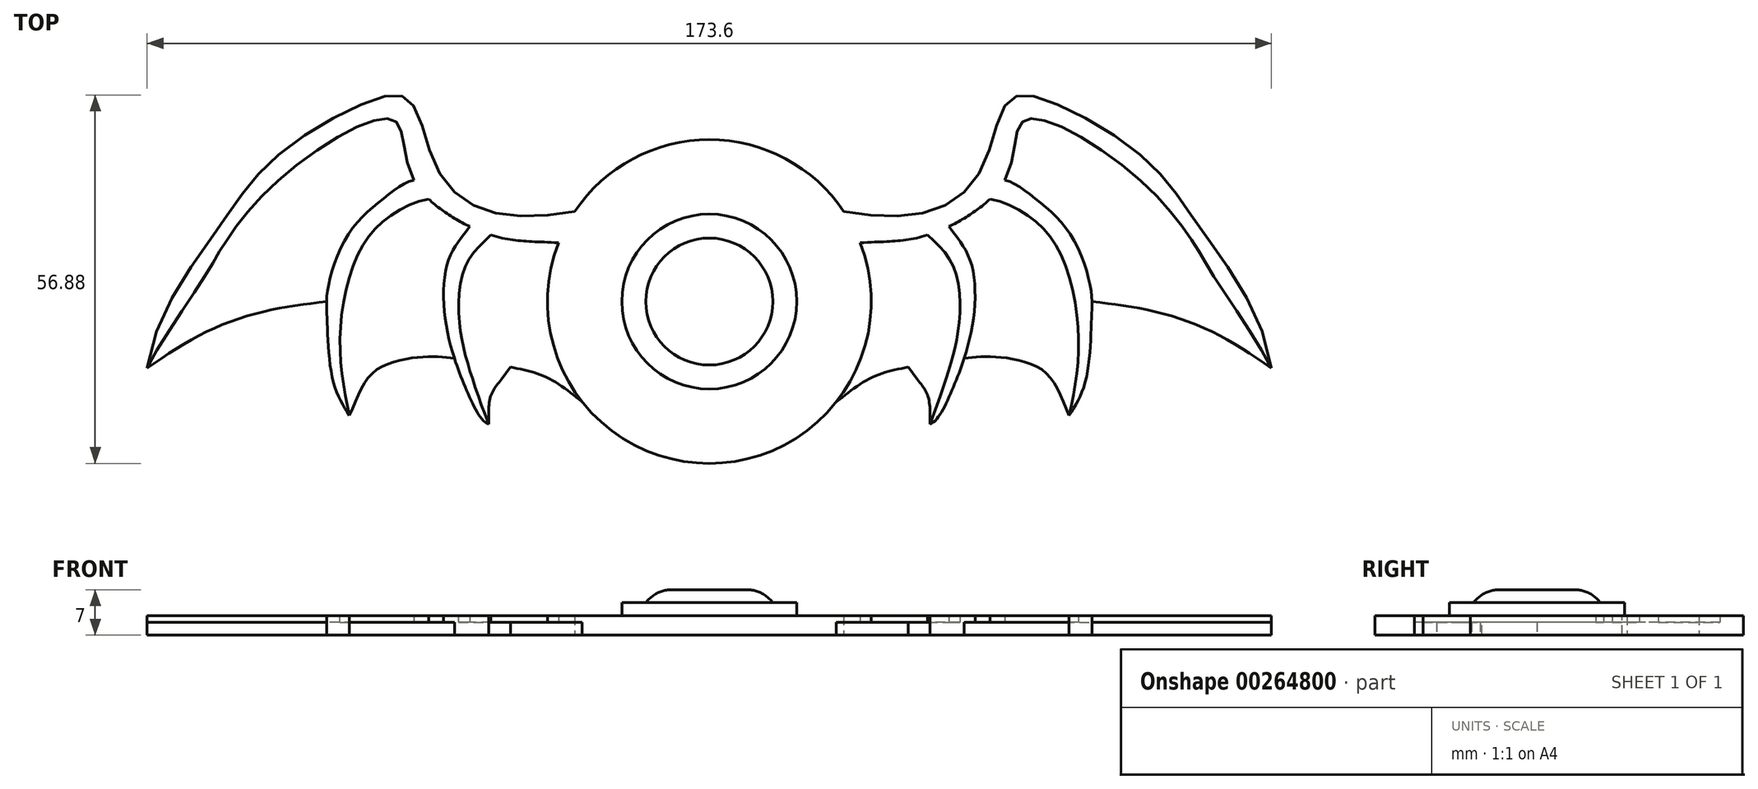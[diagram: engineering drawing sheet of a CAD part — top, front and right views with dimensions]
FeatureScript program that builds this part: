
annotation { "Feature Type Name" : "Feature", "Feature Type Description" : "" }
export const myFeature = defineFeature(function(context is Context, id is Id, definition is map)
    precondition{}
    {
        {
            var Q0;
            Q0=qCreatedBy(makeId("Top.planeOp"),FACE);
            var sketch = newSketch(context, id + "F0", { "sketchPlane" : qUnion([Q0])});
            skCircle(sketch, "E0", {"center": v(0, 0) * mm, "radius": 25 * mm});
            skLineSegment(sketch, "E1", {"start": v(0, 25) * mm, "end": v(0, -25) * mm, "construction": true});
            skFitSpline(sketch, "E2", {"points": [v(20.76, 13.92) * mm, v(34.08, 13.92) * mm, v(42, 20.48) * mm, v(46, 30.69) * mm, v(50.93, 31.48) * mm, v(67.03, 22.24) * mm, v(75.74, 11.46) * mm, v(86.8, -10.28) * mm], "startDerivative": vector(95.75, -17.53) * mm, "endDerivative": vector(18.54, -135.11) * mm});
            skFitSpline(sketch, "E3", {"points": [v(20.7, -14) * mm, v(37, -10.54) * mm, v(45, -8.07) * mm, v(66.66, 1.74) * mm, v(75.74, 11.46) * mm], "startDerivative": vector(59.46, -0.59) * mm, "endDerivative": vector(18.77, 28.66) * mm, "construction": true});
            skFitSpline(sketch, "E4", {"points": [v(23.3, 9.08) * mm, v(33.72, 10.28) * mm, v(45.64, 18.76) * mm, v(47.9, 27.18) * mm, v(51.1, 28.14) * mm, v(65.44, 19.69) * mm, v(74.45, 9.58) * mm, v(78.2, 3.43) * mm, v(86.8, -10.28) * mm], "startDerivative": vector(110.38, 5.87) * mm, "endDerivative": vector(40.39, -81.17) * mm});
            skFitSpline(sketch, "E5", {"points": [v(33.72, 10.28) * mm, v(37.86, 5.02) * mm, v(38.5, -3.9) * mm, v(37, -10.54) * mm, v(34.08, -18.9) * mm], "startDerivative": vector(21.3, -19.5) * mm, "endDerivative": vector(-13.55, -34.2) * mm});
            skFitSpline(sketch, "E6", {"points": [v(37, 11.6) * mm, v(40.25, 6.46) * mm, v(40.52, -4.24) * mm, v(37.2, -14.33) * mm, v(34.08, -18.9) * mm], "startDerivative": vector(14.85, -22) * mm, "endDerivative": vector(-16.96, -5.17) * mm});
            skFitSpline(sketch, "E7", {"points": [v(32.11, -12.01) * mm, v(33.72, -14.49) * mm, v(34.08, -18.9) * mm], "startDerivative": vector(4.43, -5.79) * mm, "endDerivative": vector(-0.15, -8.8) * mm});
            skFitSpline(sketch, "E8", {"points": [v(45.64, 18.76) * mm, v(50.26, 15.97) * mm, v(55.72, 10.44) * mm, v(58.9, 2) * mm, v(59.02, -2.64) * mm, v(58.1, -12.2) * mm, v(55.56, -17.62) * mm], "startDerivative": vector(28.21, -5.42) * mm, "endDerivative": vector(-19.1, -30.2) * mm});
            skFitSpline(sketch, "E9", {"points": [v(43.34, 15.84) * mm, v(49.55, 13.02) * mm, v(53.96, 7.9) * mm, v(56.67, -1.36) * mm, v(56.83, -10.28) * mm, v(55.56, -17.62) * mm], "startDerivative": vector(32.47, -4.35) * mm, "endDerivative": vector(-7.91, -36.84) * mm});
            skFitSpline(sketch, "E10", {"points": [v(38.97, -9.94) * mm, v(46.63, -10.28) * mm, v(52.84, -13.22) * mm, v(55.56, -17.62) * mm], "startDerivative": vector(21.38, 0.7) * mm, "endDerivative": vector(7.12, -15.9) * mm, "construction": true});
            skFitSpline(sketch, "E11", {"points": [v(59.1, 0) * mm, v(68, -1.36) * mm, v(77.72, -4.7) * mm, v(86.8, -10.28) * mm], "startDerivative": vector(27.78, -3.23) * mm, "endDerivative": vector(25.67, -17.5) * mm});
            skFitSpline(sketch, "E12", {"points": [v(19.62, -15.5) * mm, v(25.1, -11.72) * mm, v(30.69, -10.12) * mm], "startDerivative": vector(10.4, 8.3) * mm, "endDerivative": vector(11.78, 2.35) * mm});
            skFitSpline(sketch, "E13", {"points": [v(32.11, -12.01) * mm, v(30.69, -10.12) * mm], "startDerivative": vector(-1.42, 1.9) * mm, "endDerivative": vector(-1.42, 1.9) * mm});
            skFitSpline(sketch, "E14", {"points": [v(55.56, -17.62) * mm, v(52.05, -11.08) * mm, v(46.6, -8.83) * mm, v(42.13, -8.5) * mm, v(39.36, -8.79) * mm], "startDerivative": vector(-10.96, 25.87) * mm, "endDerivative": vector(-14.04, -2.02) * mm});
            skFitSpline(sketch, "E15", {"points": [v(20.76, 13.92) * mm, v(16.18, 9.49) * mm, v(19.62, -15.5) * mm], "startDerivative": vector(-16.85, -9.2) * mm, "endDerivative": vector(11.44, -45.62) * mm});
            skFitSpline(sketch, "E16.MirrorCS", {"points": [v(-20.76, 13.92) * mm, v(-16.18, 9.49) * mm, v(-19.62, -15.5) * mm], "startDerivative": vector(16.85, -9.2) * mm, "endDerivative": vector(-11.44, -45.62) * mm});
            skFitSpline(sketch, "E17.MirrorCS", {"points": [v(-23.3, 9.08) * mm, v(-33.72, 10.28) * mm, v(-45.64, 18.76) * mm, v(-47.9, 27.18) * mm, v(-51.1, 28.14) * mm, v(-65.44, 19.69) * mm, v(-74.45, 9.58) * mm, v(-78.2, 3.43) * mm, v(-86.8, -10.28) * mm], "startDerivative": vector(-110.38, 5.87) * mm, "endDerivative": vector(-40.39, -81.17) * mm});
            skFitSpline(sketch, "E18.MirrorCS", {"points": [v(-20.76, 13.92) * mm, v(-34.08, 13.92) * mm, v(-42, 20.48) * mm, v(-46, 30.69) * mm, v(-50.93, 31.48) * mm, v(-67.03, 22.24) * mm, v(-75.74, 11.46) * mm, v(-86.8, -10.28) * mm], "startDerivative": vector(-95.75, -17.53) * mm, "endDerivative": vector(-18.54, -135.11) * mm});
            skFitSpline(sketch, "E19.MirrorCS", {"points": [v(-33.72, 10.28) * mm, v(-37.86, 5.02) * mm, v(-38.5, -3.9) * mm, v(-37, -10.54) * mm, v(-34.08, -18.9) * mm], "startDerivative": vector(-21.3, -19.5) * mm, "endDerivative": vector(13.55, -34.2) * mm});
            skFitSpline(sketch, "E20.MirrorCS", {"points": [v(-37, 11.6) * mm, v(-40.25, 6.46) * mm, v(-40.52, -4.24) * mm, v(-37.2, -14.33) * mm, v(-34.08, -18.9) * mm], "startDerivative": vector(-14.85, -22) * mm, "endDerivative": vector(16.96, -5.17) * mm});
            skFitSpline(sketch, "E21.MirrorCS", {"points": [v(-43.34, 15.84) * mm, v(-49.55, 13.02) * mm, v(-53.96, 7.9) * mm, v(-56.67, -1.36) * mm, v(-56.83, -10.28) * mm, v(-55.56, -17.62) * mm], "startDerivative": vector(-32.47, -4.35) * mm, "endDerivative": vector(7.91, -36.84) * mm});
            skFitSpline(sketch, "E22.MirrorCS", {"points": [v(-45.64, 18.76) * mm, v(-50.26, 15.97) * mm, v(-55.72, 10.44) * mm, v(-58.9, 2) * mm, v(-59.02, -2.64) * mm, v(-58.1, -12.2) * mm, v(-55.56, -17.62) * mm], "startDerivative": vector(-28.21, -5.42) * mm, "endDerivative": vector(19.1, -30.2) * mm});
            skFitSpline(sketch, "E23.MirrorCS", {"points": [v(-19.62, -15.5) * mm, v(-25.1, -11.72) * mm, v(-30.69, -10.12) * mm], "startDerivative": vector(-10.4, 8.3) * mm, "endDerivative": vector(-11.78, 2.35) * mm});
            skFitSpline(sketch, "E24.MirrorCS", {"points": [v(-32.11, -12.01) * mm, v(-30.69, -10.12) * mm], "startDerivative": vector(1.42, 1.9) * mm, "endDerivative": vector(1.42, 1.9) * mm});
            skFitSpline(sketch, "E25.MirrorCS", {"points": [v(-32.11, -12.01) * mm, v(-33.72, -14.49) * mm, v(-34.08, -18.9) * mm], "startDerivative": vector(-4.43, -5.79) * mm, "endDerivative": vector(0.15, -8.8) * mm});
            skFitSpline(sketch, "E26.MirrorCS", {"points": [v(-59.1, 0) * mm, v(-68, -1.36) * mm, v(-77.72, -4.7) * mm, v(-86.8, -10.28) * mm], "startDerivative": vector(-27.78, -3.23) * mm, "endDerivative": vector(-25.67, -17.5) * mm});
            skFitSpline(sketch, "E27.MirrorCS", {"points": [v(-55.56, -17.62) * mm, v(-52.05, -11.08) * mm, v(-46.6, -8.83) * mm, v(-42.13, -8.5) * mm, v(-39.36, -8.79) * mm], "startDerivative": vector(10.96, 25.87) * mm, "endDerivative": vector(14.04, -2.02) * mm});
            skSolve(sketch);
        }
        {
            var Q0;
            {var subQ0=sQuery(id+"F0.wireOp",EDGE,"E15");Q0=makeQuery(id+"F0.imprint","IMPRINT",FACE,{"disambiguationData":[TD([[makeQuery(id+"F0.imprint","IMPRINT",EDGE,{"derivedFrom":subQ0}),-1.0]])]});}
            var Q1;
            {var subQ0=sQuery(id+"F0.wireOp",EDGE,"E15");Q1=makeQuery(id+"F0.imprint","IMPRINT",FACE,{"disambiguationData":[TD([[makeQuery(id+"F0.imprint","IMPRINT",EDGE,{"derivedFrom":subQ0}),1.0]])]});}
            var Q2;
            {var subQ0=sQuery(id+"F0.wireOp",EDGE,"E16.MirrorCS");Q2=makeQuery(id+"F0.imprint","IMPRINT",FACE,{"disambiguationData":[TD([[makeQuery(id+"F0.imprint","IMPRINT",EDGE,{"derivedFrom":subQ0}),-1.0]])]});}
            extrude(context, id + "F1", {"entities" : qUnion([Q0, Q1, Q2]), "depth" : 3 * mm, "offsetDistance" : 25 * mm});
        }
        {
            var Q0;
            Q0=qCreatedBy(makeId("Top.planeOp"),FACE);
            var sketch = newSketch(context, id + "F2", { "sketchPlane" : qUnion([Q0])});
            skCircle(sketch, "E28", {"center": v(0, 0) * mm, "radius": 13.5 * mm});
            skSolve(sketch);
        }
        {
            var Q0;
            Q0 = qSketchRegion(id + "F2", true);
            extrude(context, id + "F3", {"entities" : qUnion([Q0]), "operationType" : NewBodyOperationType.ADD, "depth" : 5 * mm, "offsetDistance" : 25 * mm});
        }
        {
            var Q0;
            Q0=qCreatedBy(makeId("Top.planeOp"),FACE);
            var sketch = newSketch(context, id + "F4", { "sketchPlane" : qUnion([Q0])});
            skCircle(sketch, "E29", {"center": v(0, 0) * mm, "radius": 9.8 * mm});
            skSolve(sketch);
        }
        {
            var Q0;
            Q0 = qSketchRegion(id + "F4", true);
            var Q1;
            Q1 = qConstructionFilter(qBodyType(qCreatedBy(id + "F4" ,EDGE), BodyType.WIRE), ConstructionObject.NO);
            extrude(context, id + "F5", {"entities" : qUnion([Q0]), "operationType" : NewBodyOperationType.ADD, "surfaceEntities" : qUnion([Q1]), "depth" : 7 * mm, "offsetDistance" : 25 * mm});
        }
        {
            var Q0;
            Q0=makeQuery(id+"F5.opExtrude","CAP_FACE",FACE,{"disambiguationData":[OSD([sQuery(id+"F4.wireOp",EDGE,"E29")])],"isStart":false});
            fillet(context, id + "F6", {"entities" : qUnion([Q0]), "radius" : 5 * mm, "tangentPropagation" : true, "allowEdgeOverflow" : false});
        }
        {
            var Q0;
            {var subQ4=sQuery(id+"F0.wireOp",EDGE,"E2");Q0=makeQuery(id+"F0.imprint","IMPRINT",FACE,{"disambiguationData":[TD([[makeQuery(id+"F0.imprint","IMPRINT",EDGE,{"derivedFrom":subQ4}),-1.0]])]});}
            var Q1;
            {var subQ0=sQuery(id+"F0.wireOp",EDGE,"E15");Q1=makeQuery(id+"F0.imprint","IMPRINT",FACE,{"disambiguationData":[TD([[makeQuery(id+"F0.imprint","IMPRINT",EDGE,{"derivedFrom":subQ0}),1.0]])]});}
            var Q2;
            {var subQ0=sQuery(id+"F0.wireOp",EDGE,"E5");Q2=makeQuery(id+"F0.imprint","IMPRINT",FACE,{"disambiguationData":[TD([[makeQuery(id+"F0.imprint","IMPRINT",EDGE,{"derivedFrom":subQ0}),-1.0]])]});}
            var Q3;
            {var subQ0=sQuery(id+"F0.wireOp",EDGE,"E5");Q3=makeQuery(id+"F0.imprint","IMPRINT",FACE,{"disambiguationData":[TD([[makeQuery(id+"F0.imprint","IMPRINT",EDGE,{"derivedFrom":subQ0}),1.0]])]});}
            var Q4;
            {var subQ3=sQuery(id+"F0.wireOp",EDGE,"E9");Q4=makeQuery(id+"F0.imprint","IMPRINT",FACE,{"disambiguationData":[TD([[makeQuery(id+"F0.imprint","IMPRINT",EDGE,{"derivedFrom":subQ3}),-1.0]])]});}
            var Q5;
            {var subQ3=sQuery(id+"F0.wireOp",EDGE,"E9");Q5=makeQuery(id+"F0.imprint","IMPRINT",FACE,{"disambiguationData":[TD([[makeQuery(id+"F0.imprint","IMPRINT",EDGE,{"derivedFrom":subQ3}),1.0]])]});}
            var Q6;
            {var subQ0=sQuery(id+"F0.wireOp",EDGE,"E11");Q6=makeQuery(id+"F0.imprint","IMPRINT",FACE,{"disambiguationData":[TD([[makeQuery(id+"F0.imprint","IMPRINT",EDGE,{"derivedFrom":subQ0}),1.0]])]});}
            var Q7;
            {var subQ1=sQuery(id+"F0.wireOp",EDGE,"E19.MirrorCS");Q7=makeQuery(id+"F0.imprint","IMPRINT",FACE,{"disambiguationData":[TD([[makeQuery(id+"F0.imprint","IMPRINT",EDGE,{"derivedFrom":subQ1}),1.0]])]});}
            var Q8;
            {var subQ3=sQuery(id+"F0.wireOp",EDGE,"E21.MirrorCS");Q8=makeQuery(id+"F0.imprint","IMPRINT",FACE,{"disambiguationData":[TD([[makeQuery(id+"F0.imprint","IMPRINT",EDGE,{"derivedFrom":subQ3}),1.0]])]});}
            var Q9;
            {var subQ0=sQuery(id+"F0.wireOp",EDGE,"E19.MirrorCS");Q9=makeQuery(id+"F0.imprint","IMPRINT",FACE,{"disambiguationData":[TD([[makeQuery(id+"F0.imprint","IMPRINT",EDGE,{"derivedFrom":subQ0}),-1.0]])]});}
            var Q10;
            {var subQ6=sQuery(id+"F0.wireOp",EDGE,"E18.MirrorCS");Q10=makeQuery(id+"F0.imprint","IMPRINT",FACE,{"disambiguationData":[TD([[makeQuery(id+"F0.imprint","IMPRINT",EDGE,{"derivedFrom":subQ6}),1.0]])]});}
            var Q11;
            {var subQ0=sQuery(id+"F0.wireOp",EDGE,"E26.MirrorCS");Q11=makeQuery(id+"F0.imprint","IMPRINT",FACE,{"disambiguationData":[TD([[makeQuery(id+"F0.imprint","IMPRINT",EDGE,{"derivedFrom":subQ0}),-1.0]])]});}
            var Q12;
            {var subQ0=sQuery(id+"F0.wireOp",EDGE,"E21.MirrorCS");Q12=makeQuery(id+"F0.imprint","IMPRINT",FACE,{"disambiguationData":[TD([[makeQuery(id+"F0.imprint","IMPRINT",EDGE,{"derivedFrom":subQ0}),-1.0]])]});}
            var Q13;
            {var subQ0=sQuery(id+"F0.wireOp",EDGE,"E16.MirrorCS");Q13=makeQuery(id+"F0.imprint","IMPRINT",FACE,{"disambiguationData":[TD([[makeQuery(id+"F0.imprint","IMPRINT",EDGE,{"derivedFrom":subQ0}),-1.0]])]});}
            extrude(context, id + "F7", {"entities" : qUnion([Q0, Q1, Q2, Q3, Q4, Q5, Q6, Q7, Q8, Q9, Q10, Q11, Q12, Q13]), "operationType" : NewBodyOperationType.ADD, "depth" : 2 * mm, "offsetDistance" : 25 * mm});
        }
        {
            var Q0;
            {var subQ4=sQuery(id+"F0.wireOp",EDGE,"E2");Q0=makeQuery(id+"F0.imprint","IMPRINT",FACE,{"disambiguationData":[TD([[makeQuery(id+"F0.imprint","IMPRINT",EDGE,{"derivedFrom":subQ4}),-1.0]])]});}
            var Q1;
            {var subQ0=sQuery(id+"F0.wireOp",EDGE,"E5");Q1=makeQuery(id+"F0.imprint","IMPRINT",FACE,{"disambiguationData":[TD([[makeQuery(id+"F0.imprint","IMPRINT",EDGE,{"derivedFrom":subQ0}),1.0]])]});}
            var Q2;
            {var subQ3=sQuery(id+"F0.wireOp",EDGE,"E9");Q2=makeQuery(id+"F0.imprint","IMPRINT",FACE,{"disambiguationData":[TD([[makeQuery(id+"F0.imprint","IMPRINT",EDGE,{"derivedFrom":subQ3}),1.0]])]});}
            var Q3;
            {var subQ6=sQuery(id+"F0.wireOp",EDGE,"E18.MirrorCS");Q3=makeQuery(id+"F0.imprint","IMPRINT",FACE,{"disambiguationData":[TD([[makeQuery(id+"F0.imprint","IMPRINT",EDGE,{"derivedFrom":subQ6}),1.0]])]});}
            var Q4;
            {var subQ0=sQuery(id+"F0.wireOp",EDGE,"E19.MirrorCS");Q4=makeQuery(id+"F0.imprint","IMPRINT",FACE,{"disambiguationData":[TD([[makeQuery(id+"F0.imprint","IMPRINT",EDGE,{"derivedFrom":subQ0}),-1.0]])]});}
            var Q5;
            {var subQ0=sQuery(id+"F0.wireOp",EDGE,"E21.MirrorCS");Q5=makeQuery(id+"F0.imprint","IMPRINT",FACE,{"disambiguationData":[TD([[makeQuery(id+"F0.imprint","IMPRINT",EDGE,{"derivedFrom":subQ0}),-1.0]])]});}
            extrude(context, id + "F8", {"entities" : qUnion([Q0, Q1, Q2, Q3, Q4, Q5]), "operationType" : NewBodyOperationType.ADD, "depth" : 3 * mm, "offsetDistance" : 25 * mm});
        }
    });
